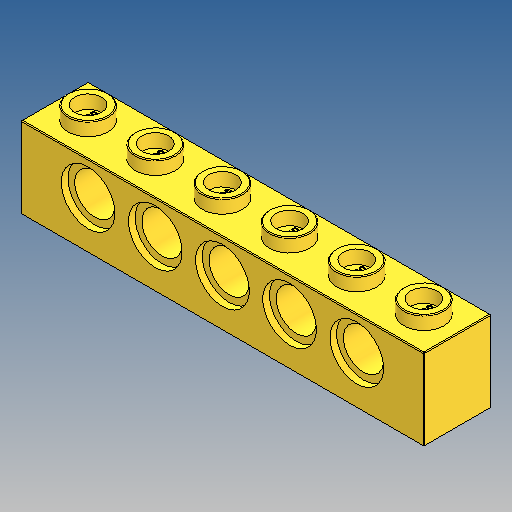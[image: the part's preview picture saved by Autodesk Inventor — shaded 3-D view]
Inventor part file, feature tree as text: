
AUTODESK INVENTOR PART (.ipt)
format: ipt  version: 2025 (Build 290162010, 162A)  size: 1,803,776 bytes
history: native  units: in
note: dims shown in document units (in); Inventor stores cm internally (conversion verified against a paired STEP export)
features: sketch x7, extrude x5, pattern_linear x3, fillet x2, other x1, plane x1, revolve x1
ambient origin geometry x8: Origin, YZ Plane, XZ Plane, XY Plane, X Axis, Y Axis, Z Axis, Center Point
bodies: Solid1 (feature_tree)
feature tree (20):
  extrude  "Extrusion1"  Depth=0.378in TaperAngle=0.0deg
  extrude  "Extrusion4"  Depth=0.063in TaperAngle=0.0deg
  extrude  "Extrusion2"  Depth=0.126in
  extrude  "Extrusion5"  Depth=0.315in
  pattern_linear  "Rectangular Pattern1"  Spacing1=0.315in  [1 undecoded]
  extrude  "Extrusion3"  Depth=0.315in
  other  "LEGO_SM:1"
  fillet  "Fillet1"  Radius=0.1575in
  pattern_linear  "Rectangular Pattern2"  Count1=6  [1 undecoded]
  fillet  "Fillet2"  Radius=0.315in
  plane  "Work Plane1"
  revolve  "Revolution1"  [1 undecoded]
  pattern_linear  "Rectangular Pattern3"  Spacing1=-0.315in  [1 undecoded]
  sketch  "Sketch2"  dims[d4=0.378in d5=0.0in d11=0.0787in d12=0.0in]
  sketch  "Sketch3"  dims[d13=0.189in d20=0.063in d21=0.0in]
  sketch  "Sketch4"  dims[d23=0.0039in d57=0.126in]
  sketch  "Sketch9"  dims[d58=1.8898in d59=0.315in]
  sketch  "Sketch10"  dims[d60=0.126in]
  sketch  "Sketch11"  dims[d61=0.063in]
  sketch  "Sketch12"  dims[d62=0.063in d63=0.315in d64=0.0in d66=1.9685in d67=0.315in d69=0.1575in d70=2.3622in d72=0.315in d73=0.0039in d74=-0.315in d75=0.2205in d76=0.0315in d77=0.189in d78=0.252in d79=90.0deg d80=1.9685in d82=0.315in d83=0.0in d84=0.0in d85=0.0in d86=0.0in d87=0.0in d88=0.1575in d89=0.315in d90=0.063in d91=0.315in d92=0.2835in d93=0.2205in d94=0.315in d95=0.0in d96=0.0055in d97=0.0513in d98=0.0197in d99=0.0245in d100=0.0055in d101=0.0097in d102=0.0197in d103=0.0245in d104=0.0197in d105=0.0111in d106=0.0124in d107=0.0245in d108=0.5428in]
note: 4 required parameter values undecoded (feature->parameter linkage not recoverable at this tier; creation-order binding heuristic only, values carry confidence <= 0.55)